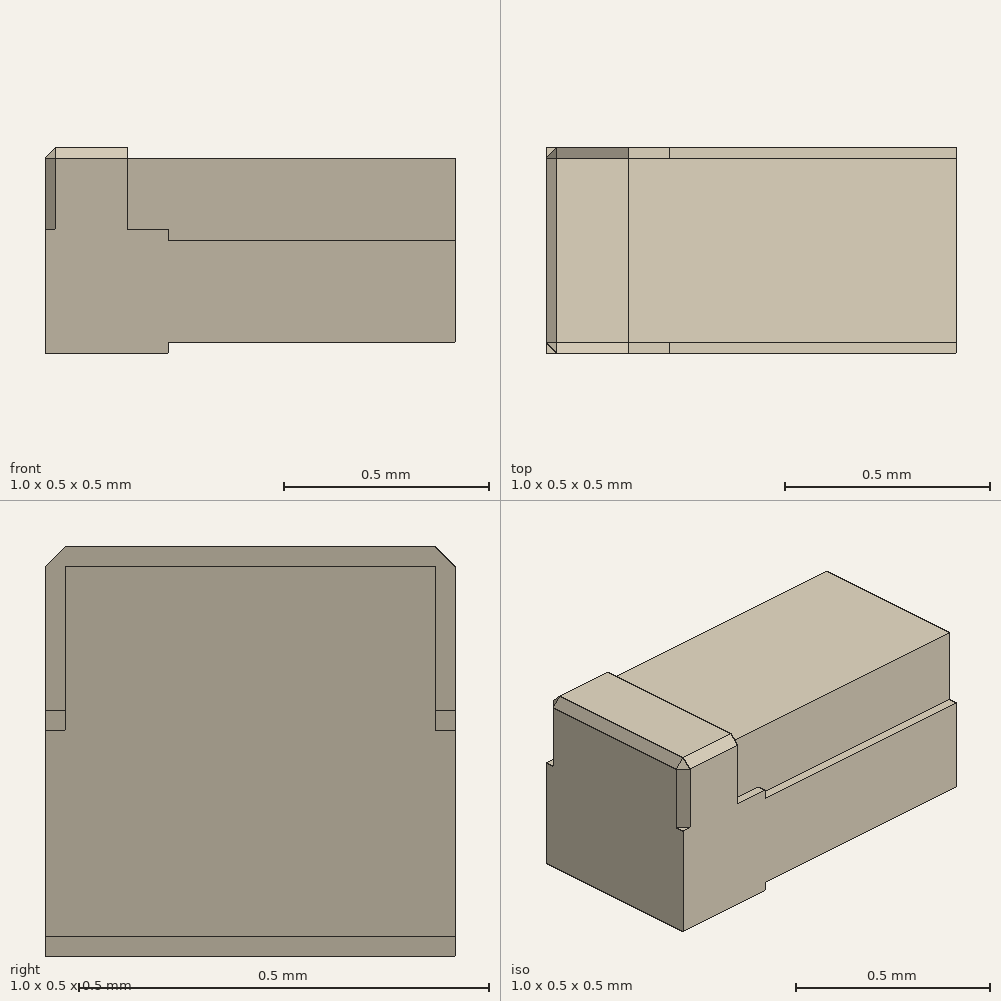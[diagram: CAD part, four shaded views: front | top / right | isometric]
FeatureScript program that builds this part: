
annotation { "Feature Type Name" : "Feature", "Feature Type Description" : "" }
export const myFeature = defineFeature(function(context is Context, id is Id, definition is map)
    precondition{}
    {
        {
            var Q0;
            Q0=qCreatedBy(makeId("Top.planeOp"),FACE);
            cPlane(context, id + "F0", {"entities" : qUnion([Q0]), "cplaneType" : CPlaneType.OFFSET, "offset" : 0.03 * mm, "width" : 150 * mm, "height" : 150 * mm});
        }
        {
            var Q0;
            Q0=qCreatedBy(id+"F0.planeOp",FACE);
            var sketch = newSketch(context, id + "F1", { "sketchPlane" : qUnion([Q0])});
            skLineSegment(sketch, "E0.bottom", {"start": v(0.48, 0.23) * mm, "end": v(-0.48, 0.23) * mm});
            skLineSegment(sketch, "E0.top", {"start": v(0.47, -0.22) * mm, "end": v(-0.48, -0.22) * mm});
            skLineSegment(sketch, "E0.left", {"start": v(0.47, 0.22) * mm, "end": v(0.47, -0.22) * mm});
            skLineSegment(sketch, "E0.right", {"start": v(-0.47, 0.22) * mm, "end": v(-0.48, -0.22) * mm});
            skPoint(sketch, "E0.middle", {"position": v(0, 0) * mm});
            skSolve(sketch);
        }
        {
            var Q0;
            Q0=qSketchRegion(id+"F1",true);
            extrude(context, id + "F2", {"entities" : qUnion([Q0]), "depth" : (0.5 - 0.03 * 2) * mm});
        }
        {
            var Q0;
            Q0=qCreatedBy(makeId("Top.planeOp"),FACE);
            var sketch = newSketch(context, id + "F3", { "sketchPlane" : qUnion([Q0])});
            skLineSegment(sketch, "E1.bottom", {"start": v(-0.53, 0.25) * mm, "end": v(-0.33, 0.25) * mm});
            skLineSegment(sketch, "E1.top", {"start": v(-0.53, -0.25) * mm, "end": v(-0.33, -0.25) * mm});
            skLineSegment(sketch, "E1.left", {"start": v(-0.53, 0.25) * mm, "end": v(-0.53, -0.25) * mm});
            skLineSegment(sketch, "E1.right", {"start": v(-0.33, 0.25) * mm, "end": v(-0.33, -0.25) * mm});
            skPoint(sketch, "E2", {"position": v(-0.53, 0) * mm});
            skSolve(sketch);
        }
        {
            var Q0;
            Q0=qSketchRegion(id+"F3",true);
            extrude(context, id + "F4", {"entities" : qUnion([Q0]), "operationType" : NewBodyOperationType.ADD, "depth" : 0.5 * mm});
        }
        {
            var Q0;
            Q0=makeQuery(id+"F4.opExtrude","SWEPT_FACE",FACE,{"disambiguationData":[OSD([sQuery(id+"F3.wireOp",EDGE,"E1.left")])]});
            var Q1;
            Q1=makeQuery(id+"FBoT5Qqc3x7R15t_1.1.F4.opExtrude","SWEPT_FACE",FACE,{"disambiguationData":[OSD([sQuery(id+"F3.wireOp",EDGE,"E1.left")])]});
            var Q2;
            Q2=makeQuery(id+"F4.opExtrude","CAP_EDGE",EDGE,{"disambiguationData":[OSD([sQuery(id+"F3.wireOp",EDGE,"E1.bottom")])],"isStart":false});
            var Q3;
            Q3=makeQuery(id+"F4.opExtrude","CAP_EDGE",EDGE,{"disambiguationData":[OSD([sQuery(id+"F3.wireOp",EDGE,"E1.bottom")])],"isStart":true});
            var Q4;
            Q4=makeQuery(id+"F4.opExtrude","CAP_EDGE",EDGE,{"disambiguationData":[OSD([sQuery(id+"F3.wireOp",EDGE,"E1.top")])],"isStart":false});
            var Q5;
            Q5=makeQuery(id+"F4.opExtrude","CAP_EDGE",EDGE,{"disambiguationData":[OSD([sQuery(id+"F3.wireOp",EDGE,"E1.top")])],"isStart":true});
            var Q6;
            Q6=makeQuery(id+"FBoT5Qqc3x7R15t_1.1.F4.opExtrude","CAP_EDGE",EDGE,{"disambiguationData":[OSD([sQuery(id+"F3.wireOp",EDGE,"E1.top")])],"isStart":true});
            var Q7;
            Q7=makeQuery(id+"FBoT5Qqc3x7R15t_1.1.F4.opExtrude","CAP_EDGE",EDGE,{"disambiguationData":[OSD([sQuery(id+"F3.wireOp",EDGE,"E1.top")])],"isStart":false});
            var Q8;
            Q8=makeQuery(id+"FBoT5Qqc3x7R15t_1.1.F4.opExtrude","CAP_EDGE",EDGE,{"disambiguationData":[OSD([sQuery(id+"F3.wireOp",EDGE,"E1.bottom")])],"isStart":false});
            var Q9;
            Q9=makeQuery(id+"FBoT5Qqc3x7R15t_1.1.F4.opExtrude","CAP_EDGE",EDGE,{"disambiguationData":[OSD([sQuery(id+"F3.wireOp",EDGE,"E1.bottom")])],"isStart":true});
            chamfer(context, id + "F5", {"entities" : qUnion([Q0, Q1, Q2, Q3, Q4, Q5, Q6, Q7, Q8, Q9]), "width" : 0.03 * mm, "tangentPropagation" : true});
        }
        {
            var Q0;
            Q0=qCreatedBy(id+"F0.planeOp",FACE);
            var sketch = newSketch(context, id + "F6", { "sketchPlane" : qUnion([Q0])});
            skLineSegment(sketch, "E3.bottom", {"start": v(0.47, -0.25) * mm, "end": v(-0.47, -0.25) * mm});
            skLineSegment(sketch, "E3.top", {"start": v(0.47, 0.25) * mm, "end": v(-0.47, 0.25) * mm});
            skLineSegment(sketch, "E3.left", {"start": v(0.47, -0.25) * mm, "end": v(0.47, 0.25) * mm});
            skLineSegment(sketch, "E3.right", {"start": v(-0.47, -0.25) * mm, "end": v(-0.47, 0.25) * mm});
            skPoint(sketch, "E3.middle", {"position": v(0, 0) * mm});
            skSolve(sketch);
        }
        {
            var Q0;
            Q0=qSketchRegion(id+"F6",true);
            extrude(context, id + "F7", {"entities" : qUnion([Q0]), "depth" : (0.3 - 0.03 * 2) * mm});
        }
        {
            var Q0;
            Q0=qCreatedBy(makeId("Top.planeOp"),FACE);
            var sketch = newSketch(context, id + "F8", { "sketchPlane" : qUnion([Q0])});
            skLineSegment(sketch, "E4.bottom", {"start": v(-0.53, -0.25) * mm, "end": v(-0.23, -0.25) * mm});
            skLineSegment(sketch, "E4.top", {"start": v(-0.53, 0.25) * mm, "end": v(-0.23, 0.25) * mm});
            skLineSegment(sketch, "E4.left", {"start": v(-0.53, -0.25) * mm, "end": v(-0.53, 0.25) * mm});
            skLineSegment(sketch, "E4.right", {"start": v(-0.23, -0.25) * mm, "end": v(-0.23, 0.25) * mm});
            skPoint(sketch, "E5", {"position": v(-0.53, 0) * mm});
            skSolve(sketch);
        }
        {
            var Q0;
            Q0=qSketchRegion(id+"F8",true);
            extrude(context, id + "F9", {"entities" : qUnion([Q0]), "operationType" : NewBodyOperationType.ADD, "depth" : 0.3 * mm});
        }
    });
